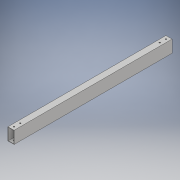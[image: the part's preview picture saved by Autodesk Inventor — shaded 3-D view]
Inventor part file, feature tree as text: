
AUTODESK INVENTOR PART (.ipt)
format: ipt  version: 2018 (Build 220112000, 112)  size: 118,784 bytes
history: native  units: in
note: dims shown in document units (in); Inventor stores cm internally (conversion verified against a paired STEP export)
features: extrude x2, sketch x2
ambient origin geometry x8: Origin, YZ Plane, XZ Plane, XY Plane, X Axis, Y Axis, Z Axis, Center Point
bodies: Solid1 (feature_tree)
feature tree (4):
  extrude  "Extrusion1"  Depth=2.0in
  extrude  "Extrusion2"  Depth=25.722in TaperAngle=0.0deg
  sketch  "Sketch1"  dims[d0=1.0in d1=2.0in]
  sketch  "Sketch2"  dims[d2=0.0625in d3=25.722in d4=0.0in d5=0.5in d6=1.0in d7=0.5in d8=1.0in d9=0.2031in d10=25.722in d11=0.0in]
